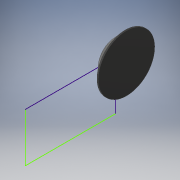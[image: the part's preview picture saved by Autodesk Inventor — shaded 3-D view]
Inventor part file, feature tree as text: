
AUTODESK INVENTOR PART (.ipt)
format: ipt  version: 2018 (Build 220112000, 112)  size: 147,456 bytes
history: native  units: mm
features: sketch x7, extrude x2, revolve x1
ambient origin geometry x8: Origin, YZ Plane, XZ Plane, XY Plane, X Axis, Y Axis, Z Axis, Center Point
bodies: Solid1 (feature_tree)
feature tree (10):
  revolve  "Revolution1"  [1 undecoded]
  extrude  "Extrusion1"  TaperAngle=90.0deg  [1 undecoded]
  sketch  "Sketch4"  dims[d11=24.0mm d12=7.5mm]
  sketch  "Sketch6"  dims[d13=7.4mm]
  sketch  "Sketch7"  dims[d14=10.0mm d15=0.0mm]
  extrude  "Extrusion2"  Depth=7.5mm
  sketch  "Sketch10"  dims[d18=3.0mm d19=0.0mm]
  sketch  "Sketch2"  dims[d4=65.0mm d5=22.0mm]
  sketch  "Sketch3"  dims[d6=40.3mm d7=90.0deg]
  sketch  "Sketch8"  dims[d17=5.0mm]
note: 2 required parameter values undecoded (feature->parameter linkage not recoverable at this tier; creation-order binding heuristic only, values carry confidence <= 0.55)